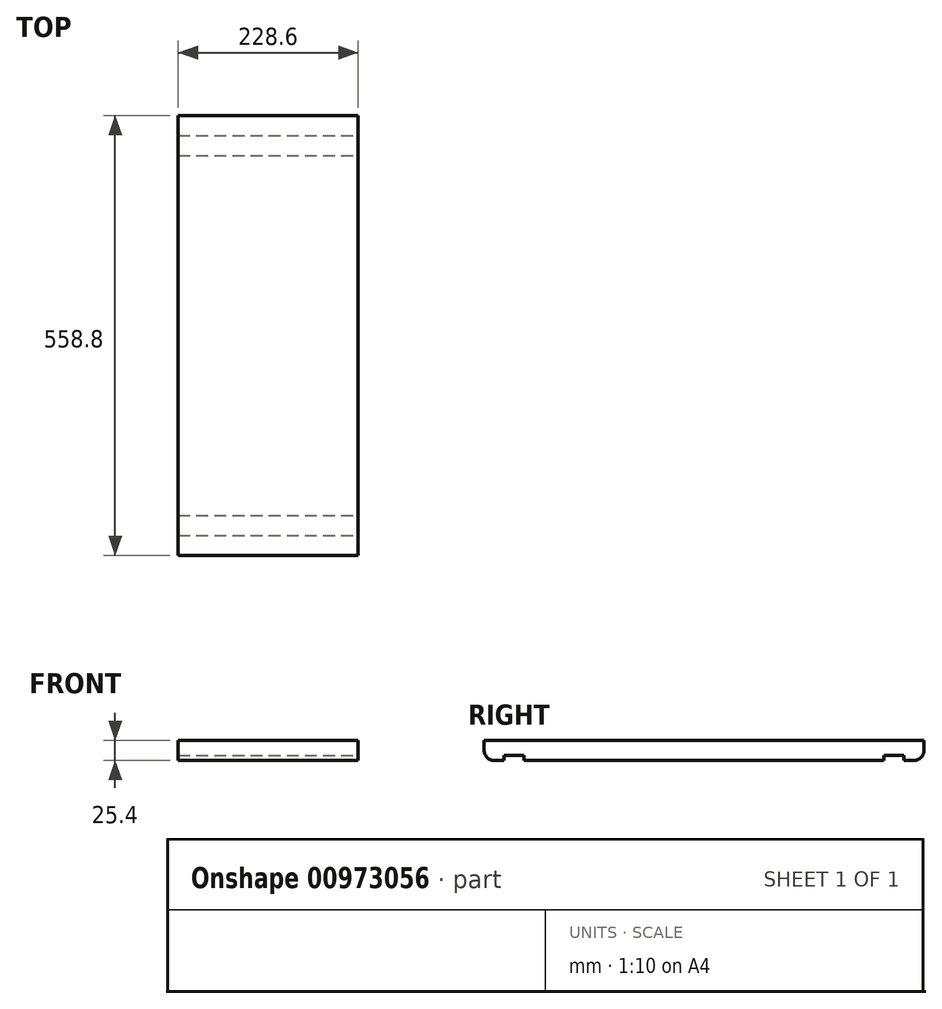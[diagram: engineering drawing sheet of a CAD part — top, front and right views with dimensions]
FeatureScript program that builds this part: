
annotation { "Feature Type Name" : "Feature", "Feature Type Description" : "" }
export const myFeature = defineFeature(function(context is Context, id is Id, definition is map)
    precondition{}
    {
        {
            var Q0;
            Q0=qCreatedBy(makeId("Top.planeOp"),FACE);
            var sketch = newSketch(context, id + "F0", { "sketchPlane" : qUnion([Q0])});
            skLineSegment(sketch, "E0.bottom", {"start": v(114.3, 279.4) * mm, "end": v(-114.3, 279.4) * mm});
            skLineSegment(sketch, "E0.top", {"start": v(114.3, -279.4) * mm, "end": v(-114.3, -279.4) * mm});
            skLineSegment(sketch, "E0.left", {"start": v(114.3, 279.4) * mm, "end": v(114.3, -279.4) * mm});
            skLineSegment(sketch, "E0.right", {"start": v(-114.3, 279.4) * mm, "end": v(-114.3, -279.4) * mm});
            skPoint(sketch, "E0.middle", {"position": v(0, 0) * mm});
            skSolve(sketch);
        }
        {
            var Q0;
            Q0=makeQuery(id+"F0.imprint","IMPRINT",FACE,{"disambiguationData":[TD([[makeQuery(id+"F0.imprint","IMPRINT",EDGE,{"derivedFrom":sQuery(id+"F0.wireOp",EDGE,"E0.bottom")}),1.0]])]});
            extrude(context, id + "F1", {"entities" : qUnion([Q0]), "depth" : 25.4 * mm, "offsetDistance" : 25.4 * mm});
        }
        {
            var Q0;
            Q0=makeQuery(id+"F1.opExtrude","CAP_FACE",FACE,{"disambiguationData":[OSD([sQuery(id+"F0.wireOp",EDGE,"E0.bottom"),sQuery(id+"F0.wireOp",EDGE,"E0.top"),sQuery(id+"F0.wireOp",EDGE,"E0.left"),sQuery(id+"F0.wireOp",EDGE,"E0.right")])],"isStart":true});
            var sketch = newSketch(context, id + "F2", { "sketchPlane" : qUnion([Q0])});
            skLineSegment(sketch, "E1.bottom", {"start": v(-114.3, 254) * mm, "end": v(114.3, 254) * mm});
            skLineSegment(sketch, "E1.top", {"start": v(-114.3, 228.6) * mm, "end": v(114.3, 228.6) * mm});
            skLineSegment(sketch, "E1.left", {"start": v(-114.3, 254) * mm, "end": v(-114.3, 228.6) * mm});
            skLineSegment(sketch, "E1.right", {"start": v(114.3, 254) * mm, "end": v(114.3, 228.6) * mm});
            skSolve(sketch);
        }
        {
            var Q0;
            Q0=makeQuery(id+"F2.imprint","IMPRINT",FACE,{"disambiguationData":[TD([[makeQuery(id+"F2.imprint","IMPRINT",EDGE,{"derivedFrom":sQuery(id+"F2.wireOp",EDGE,"E1.bottom")}),-1.0]])]});
            extrude(context, id + "F3", {"entities" : qUnion([Q0]), "operationType" : NewBodyOperationType.REMOVE, "oppositeDirection" : true, "depth" : 6.35 * mm, "offsetDistance" : 25.4 * mm});
        }
        {
            var Q0;
            {var subQ0=sQuery(id+"F0.wireOp",EDGE,"E0.bottom");var subQ1=sQuery(id+"F0.wireOp",EDGE,"E0.right");var subQ2=sQuery(id+"F0.wireOp",EDGE,"E0.left");Q0=makeQuery(id+"F3.boolean.opBoolean","SPLIT",FACE,{"disambiguationData":[TD([makeQuery(id+"F1.opExtrude","SWEPT_FACE",FACE,{"disambiguationData":[OSD([subQ0])]})])],"derivedFrom":makeQuery(id+"F1.opExtrude","CAP_FACE",FACE,{"disambiguationData":[OSD([subQ0,sQuery(id+"F0.wireOp",EDGE,"E0.top"),subQ2,subQ1])],"isStart":true})});}
            var sketch = newSketch(context, id + "F4", { "sketchPlane" : qUnion([Q0])});
            skLineSegment(sketch, "E2.bottom", {"start": v(-114.3, -228.6) * mm, "end": v(114.3, -228.6) * mm});
            skLineSegment(sketch, "E2.top", {"start": v(-114.3, -254) * mm, "end": v(114.3, -254) * mm});
            skLineSegment(sketch, "E2.left", {"start": v(-114.3, -228.6) * mm, "end": v(-114.3, -254) * mm});
            skLineSegment(sketch, "E2.right", {"start": v(114.3, -228.6) * mm, "end": v(114.3, -254) * mm});
            skSolve(sketch);
        }
        {
            var Q0;
            Q0=makeQuery(id+"F4.imprint","IMPRINT",FACE,{"disambiguationData":[TD([[makeQuery(id+"F4.imprint","IMPRINT",EDGE,{"derivedFrom":sQuery(id+"F4.wireOp",EDGE,"E2.bottom")}),-1.0]])]});
            extrude(context, id + "F5", {"entities" : qUnion([Q0]), "operationType" : NewBodyOperationType.REMOVE, "oppositeDirection" : true, "depth" : 6.35 * mm, "offsetDistance" : 25.4 * mm});
        }
        {
            var Q0;
            Q0=makeQuery(id+"F1.opExtrude","CAP_EDGE",EDGE,{"disambiguationData":[OSD([sQuery(id+"F0.wireOp",EDGE,"E0.top")])],"isStart":true});
            var Q1;
            Q1=makeQuery(id+"F1.opExtrude","CAP_EDGE",EDGE,{"disambiguationData":[OSD([sQuery(id+"F0.wireOp",EDGE,"E0.bottom")])],"isStart":true});
            fillet(context, id + "F6", {"entities" : qUnion([Q0, Q1]), "radius" : 12.7 * mm, "tangentPropagation" : true, "allowEdgeOverflow" : false});
        }
    });
